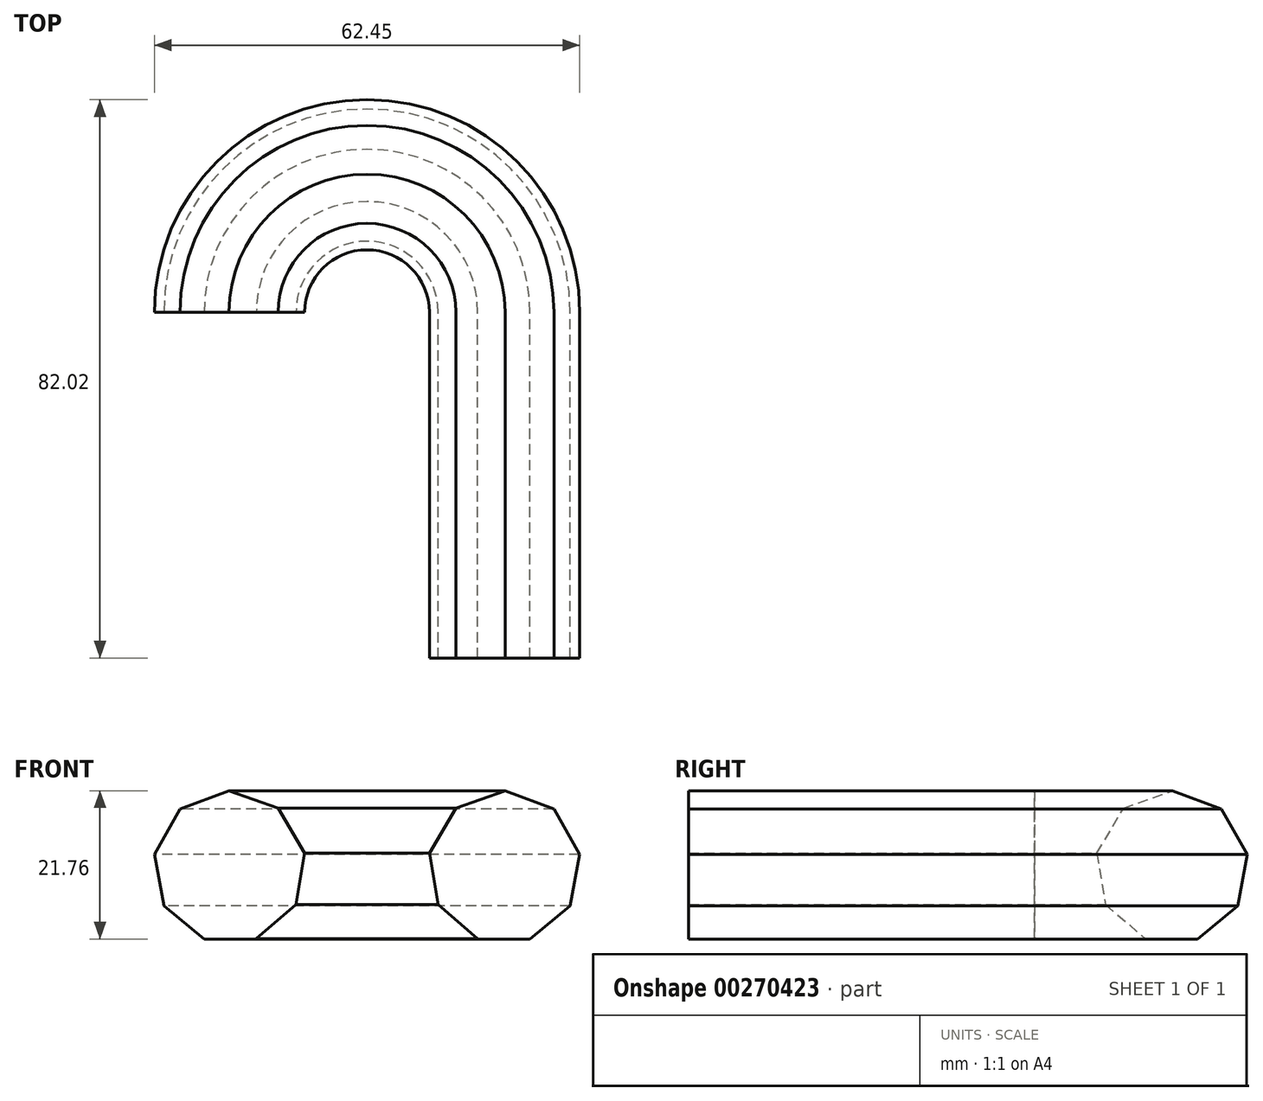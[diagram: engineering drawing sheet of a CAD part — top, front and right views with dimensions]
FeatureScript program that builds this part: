
annotation { "Feature Type Name" : "Feature", "Feature Type Description" : "" }
export const myFeature = defineFeature(function(context is Context, id is Id, definition is map)
    precondition{}
    {
        {
            var Q0;
            Q0=qCreatedBy(makeId("Front.planeOp"),FACE);
            var sketch = newSketch(context, id + "F0", { "sketchPlane" : qUnion([Q0])});
            skCircle(sketch, "E0.cCircle", {"center": v(0, 0) * mm, "radius": 10.53 * mm, "construction": true});
            skLineSegment(sketch, "E0.0", {"start": v(7.27, 8.52) * mm, "end": v(11.05, 1.86) * mm});
            skLineSegment(sketch, "E0.1", {"start": v(11.05, 1.86) * mm, "end": v(9.66, -5.68) * mm});
            skLineSegment(sketch, "E0.2", {"start": v(9.66, -5.68) * mm, "end": v(3.75, -10.56) * mm});
            skLineSegment(sketch, "E0.3", {"start": v(3.75, -10.56) * mm, "end": v(-3.92, -10.5) * mm});
            skLineSegment(sketch, "E0.4", {"start": v(-3.92, -10.5) * mm, "end": v(-9.75, -5.52) * mm});
            skLineSegment(sketch, "E0.5", {"start": v(-9.75, -5.52) * mm, "end": v(-11.02, 2.03) * mm});
            skLineSegment(sketch, "E0.6", {"start": v(-11.02, 2.03) * mm, "end": v(-7.13, 8.64) * mm});
            skLineSegment(sketch, "E0.7", {"start": v(-7.13, 8.64) * mm, "end": v(0.1, 11.2) * mm});
            skLineSegment(sketch, "E0.8", {"start": v(0.1, 11.2) * mm, "end": v(7.27, 8.52) * mm});
            skPoint(sketch, "E0.0.midPoint", {"position": v(9.16, 5.19) * mm});
            skSolve(sketch);
        }
        {
            var Q0;
            Q0=qCreatedBy(makeId("Top.planeOp"),FACE);
            var sketch = newSketch(context, id + "F1", { "sketchPlane" : qUnion([Q0])});
            skLineSegment(sketch, "E1", {"start": v(0, 0) * mm, "end": v(0, 50.8) * mm});
            skArc(sketch, "E2", {"start": v(0, 50.8) * mm, "mid": v(-20.18, 70.98) * mm, "end": v(-40.36, 50.8) * mm});
            skSolve(sketch);
        }
        {
            var Q0;
            Q0=makeQuery(id+"F0.imprint","IMPRINT",FACE,{"disambiguationData":[TD([[makeQuery(id+"F0.imprint","IMPRINT",EDGE,{"derivedFrom":sQuery(id+"F0.wireOp",EDGE,"E0.0")}),-1.0]])]});
            var Q1;
            Q1=sQuery(id+"F1.wireOp",EDGE,"E1");
            var Q2;
            Q2=sQuery(id+"F1.wireOp",EDGE,"E2");
            sweep(context, id + "F2", {"profiles" : qUnion([Q0]), "path" : qUnion([Q1, Q2])});
        }
    });
